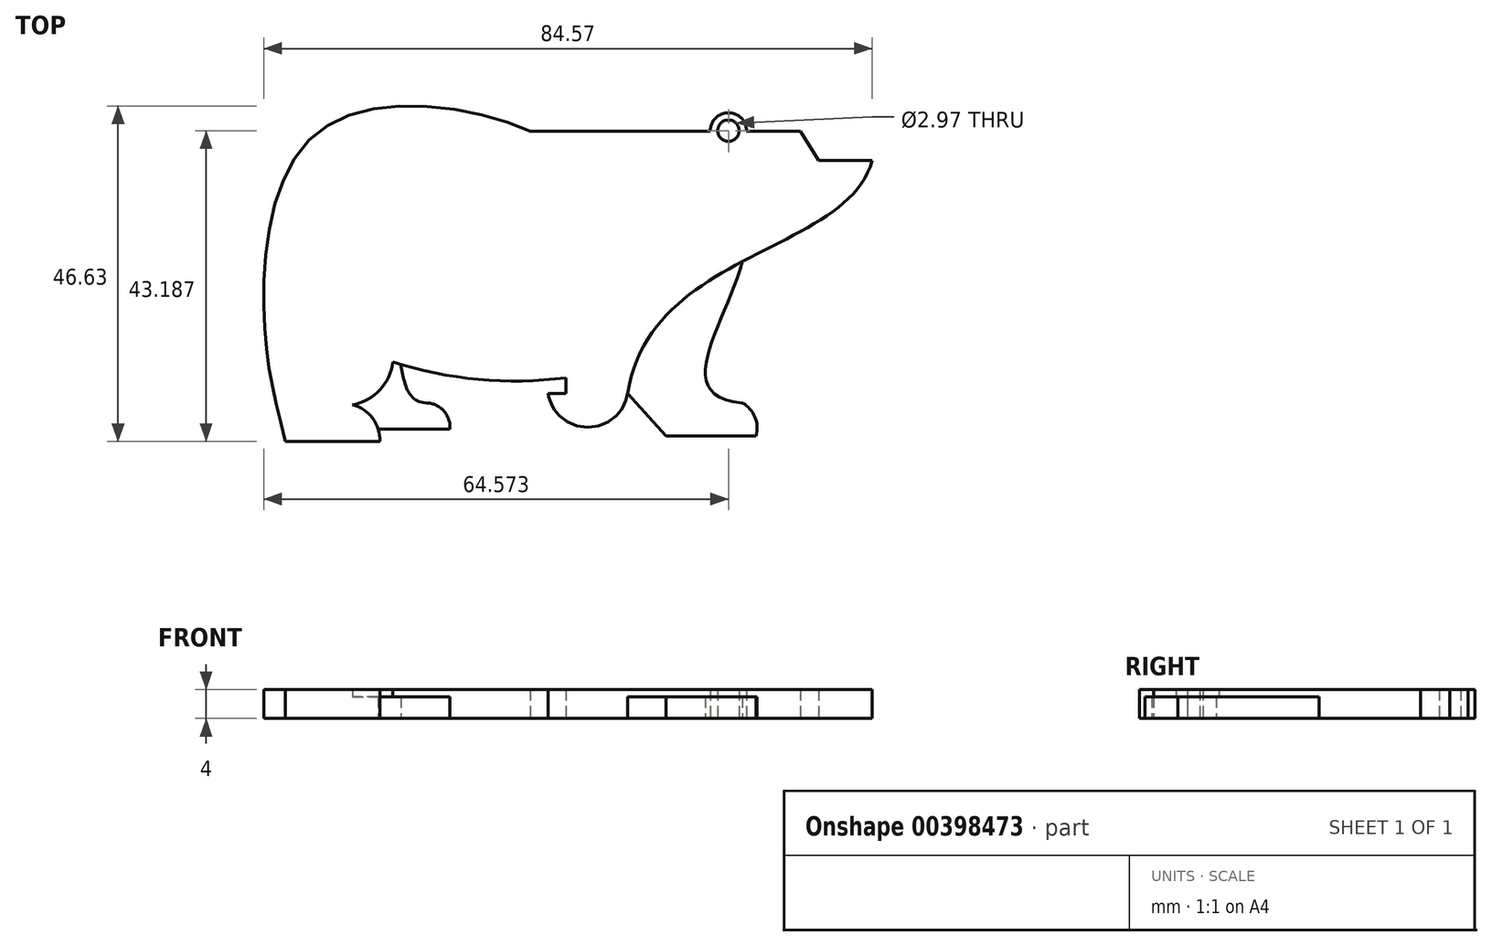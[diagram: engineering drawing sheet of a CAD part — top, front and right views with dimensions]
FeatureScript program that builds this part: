
annotation { "Feature Type Name" : "Feature", "Feature Type Description" : "" }
export const myFeature = defineFeature(function(context is Context, id is Id, definition is map)
    precondition{}
    {
        {
            var Q0;
            Q0=qCreatedBy(makeId("Top.planeOp"),FACE);
            var sketch = newSketch(context, id + "F0", { "sketchPlane" : qUnion([Q0])});
            skLineSegment(sketch, "E0", {"start": v(-35.17, 3.76) * mm, "end": v(-10.17, 3.76) * mm});
            skArc(sketch, "E1", {"start": v(-5.17, 3.76) * mm, "mid": v(-7.67, 6.32) * mm, "end": v(-10.17, 3.76) * mm});
            skLineSegment(sketch, "E2", {"start": v(-5.17, 3.76) * mm, "end": v(2.33, 3.76) * mm});
            skLineSegment(sketch, "E3", {"start": v(2.33, 3.76) * mm, "end": v(4.85, -0.33) * mm});
            skLineSegment(sketch, "E4", {"start": v(4.85, -0.33) * mm, "end": v(12.33, -0.33) * mm});
            skFitSpline(sketch, "E5", {"points": [v(12.33, -0.33) * mm, v(-21.67, -32.68) * mm], "startDerivative": vector(-10.86, -38.73) * mm, "endDerivative": vector(-9.57, -59.59) * mm});
            skArc(sketch, "E6", {"start": v(-32.74, -32.68) * mm, "mid": v(-27.2, -37.4) * mm, "end": v(-21.67, -32.68) * mm});
            skLineSegment(sketch, "E7", {"start": v(-21.67, -32.68) * mm, "end": v(-16.33, -38.6) * mm});
            skLineSegment(sketch, "E8", {"start": v(-16.33, -38.6) * mm, "end": v(-3.83, -38.6) * mm});
            skArc(sketch, "E9", {"start": v(-3.83, -38.6) * mm, "mid": v(-3.99, -35.98) * mm, "end": v(-5.74, -34.01) * mm});
            skFitSpline(sketch, "E10", {"points": [v(-5.74, -34.01) * mm, v(-5.74, -14.38) * mm], "startDerivative": vector(-30.9, 2.58) * mm, "endDerivative": vector(6.87, 25.42) * mm});
            skLineSegment(sketch, "E11", {"start": v(-32.74, -32.68) * mm, "end": v(-30.25, -32.68) * mm});
            skLineSegment(sketch, "E12", {"start": v(-30.25, -32.68) * mm, "end": v(-30.25, -30.53) * mm});
            skArc(sketch, "E13", {"start": v(-54.32, -28.31) * mm, "mid": v(-42.4, -30.75) * mm, "end": v(-30.25, -30.53) * mm});
            skArc(sketch, "E14", {"start": v(-59.88, -34.27) * mm, "mid": v(-56.1, -32.22) * mm, "end": v(-54.32, -28.31) * mm});
            skArc(sketch, "E15", {"start": v(-56.1, -39.37) * mm, "mid": v(-57.11, -36.17) * mm, "end": v(-59.88, -34.27) * mm});
            skPoint(sketch, "E15.startSnap0", {"position": v(-56.1, -32.22) * mm});
            skLineSegment(sketch, "E16", {"start": v(-56.1, -39.37) * mm, "end": v(-69.22, -39.37) * mm});
            skFitSpline(sketch, "E17", {"points": [v(-35.17, 3.76) * mm, v(-64.53, 3.76) * mm, v(-72.18, -22.02) * mm, v(-69.22, -39.37) * mm], "startDerivative": vector(-70.52, 30.67) * mm, "endDerivative": vector(15.82, -62.7) * mm});
            skLineSegment(sketch, "E18", {"start": v(-56.35, -37.65) * mm, "end": v(-46.35, -37.65) * mm});
            skArc(sketch, "E19", {"start": v(-46.35, -37.65) * mm, "mid": v(-47.23, -35.13) * mm, "end": v(-49.64, -34.01) * mm});
            skFitSpline(sketch, "E20", {"points": [v(-53.2, -28.66) * mm, v(-49.64, -34.01) * mm], "startDerivative": vector(1.22, -6.35) * mm, "endDerivative": vector(8.42, -0.26) * mm});
            skCircle(sketch, "E21", {"center": v(-7.67, 3.82) * mm, "radius": 1.49 * mm});
            skSolve(sketch);
        }
        {
            var Q0;
            Q0=makeQuery(id+"F0.imprint","IMPRINT",FACE,{"disambiguationData":[TD([[makeQuery(id+"F0.imprint","IMPRINT",EDGE,{"derivedFrom":sQuery(id+"F0.wireOp",EDGE,"E0")}),-1.0]])]});
            extrude(context, id + "F1", {"entities" : qUnion([Q0]), "depth" : 4 * mm});
        }
        {
            var Q0;
            {var subQ0=sQuery(id+"F0.wireOp",EDGE,"E7");Q0=makeQuery(id+"F0.imprint","IMPRINT",FACE,{"disambiguationData":[TD([[makeQuery(id+"F0.imprint","IMPRINT",EDGE,{"derivedFrom":subQ0}),1.0]])]});}
            extrude(context, id + "F2", {"entities" : qUnion([Q0]), "operationType" : NewBodyOperationType.ADD, "depth" : 3 * mm});
        }
        {
            var Q0;
            {var subQ1=sQuery(id+"F0.wireOp",EDGE,"E14");Q0=makeQuery(id+"F0.imprint","IMPRINT",FACE,{"disambiguationData":[TD([[makeQuery(id+"F0.imprint","IMPRINT",EDGE,{"derivedFrom":subQ1}),-1.0]])]});}
            extrude(context, id + "F3", {"entities" : qUnion([Q0]), "operationType" : NewBodyOperationType.ADD, "depth" : 3 * mm});
        }
    });
